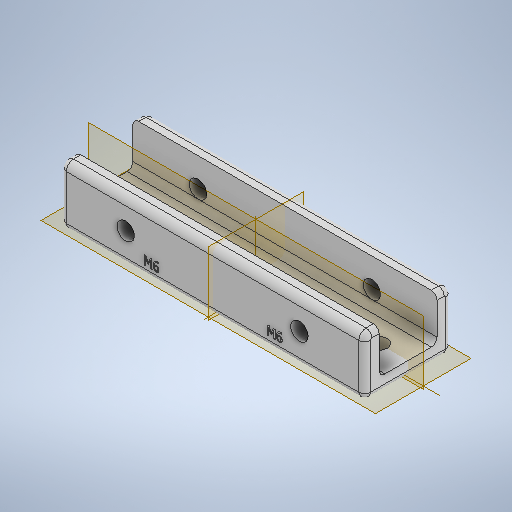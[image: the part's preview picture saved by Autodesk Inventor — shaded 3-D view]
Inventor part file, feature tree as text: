
AUTODESK INVENTOR PART (.ipt)
format: ipt  version: 2025 (Build 290162000, 162)  size: 679,936 bytes
history: native  units: mm
features: sketch x6, hole x3, emboss x2, extrude x1, fillet x1, mirror x1
ambient origin geometry x8: Origin, YZ Plane, XZ Plane, XY Plane, X Axis, Y Axis, Z Axis, Center Point
bodies: Body1 (feature_tree)
feature tree (14):
  extrude  "Extrusion2"  Depth=30.0mm
  fillet  "Fillet2"  Radius=5.0mm
  hole  "Hole4"  [1 undecoded]
  hole  "Hole5"  [1 undecoded]
  hole  "Hole6"  [1 undecoded]
  mirror  "Mirror4"
  emboss  "Emboss3"
  emboss  "Emboss4"
  sketch  "Sketch6"  dims[d35=20.0mm d36=30.0mm d37=5.0mm]
  sketch  "Sketch7"  dims[d38=2.0mm d39=2.5mm]
  sketch  "Sketch8"  dims[d40=105.0mm d41=0.0mm d42=2.0mm]
  sketch  "Sketch9"  dims[d43=6.35mm d44=6.0mm d45=4.0mm d46=2.0mm d47=90.0deg d48=8.0mm d49=20.594885mm]
  sketch  "Sketch10"  dims[d50=6.0mm d51=6.0mm d52=4.0mm d53=2.0mm d54=90.0deg d55=8.0mm d56=20.594885mm d57=42.25mm]
  sketch  "Sketch11"  dims[d58=6.0mm d59=6.0mm d60=4.0mm d61=2.0mm d62=90.0deg d63=8.0mm d64=20.594885mm d65=10.0mm d66=30.0mm d67=1.5mm d68=0.0mm d69=1.5mm d70=0.0mm]
note: 3 required parameter values undecoded (feature->parameter linkage not recoverable at this tier; creation-order binding heuristic only, values carry confidence <= 0.55)
